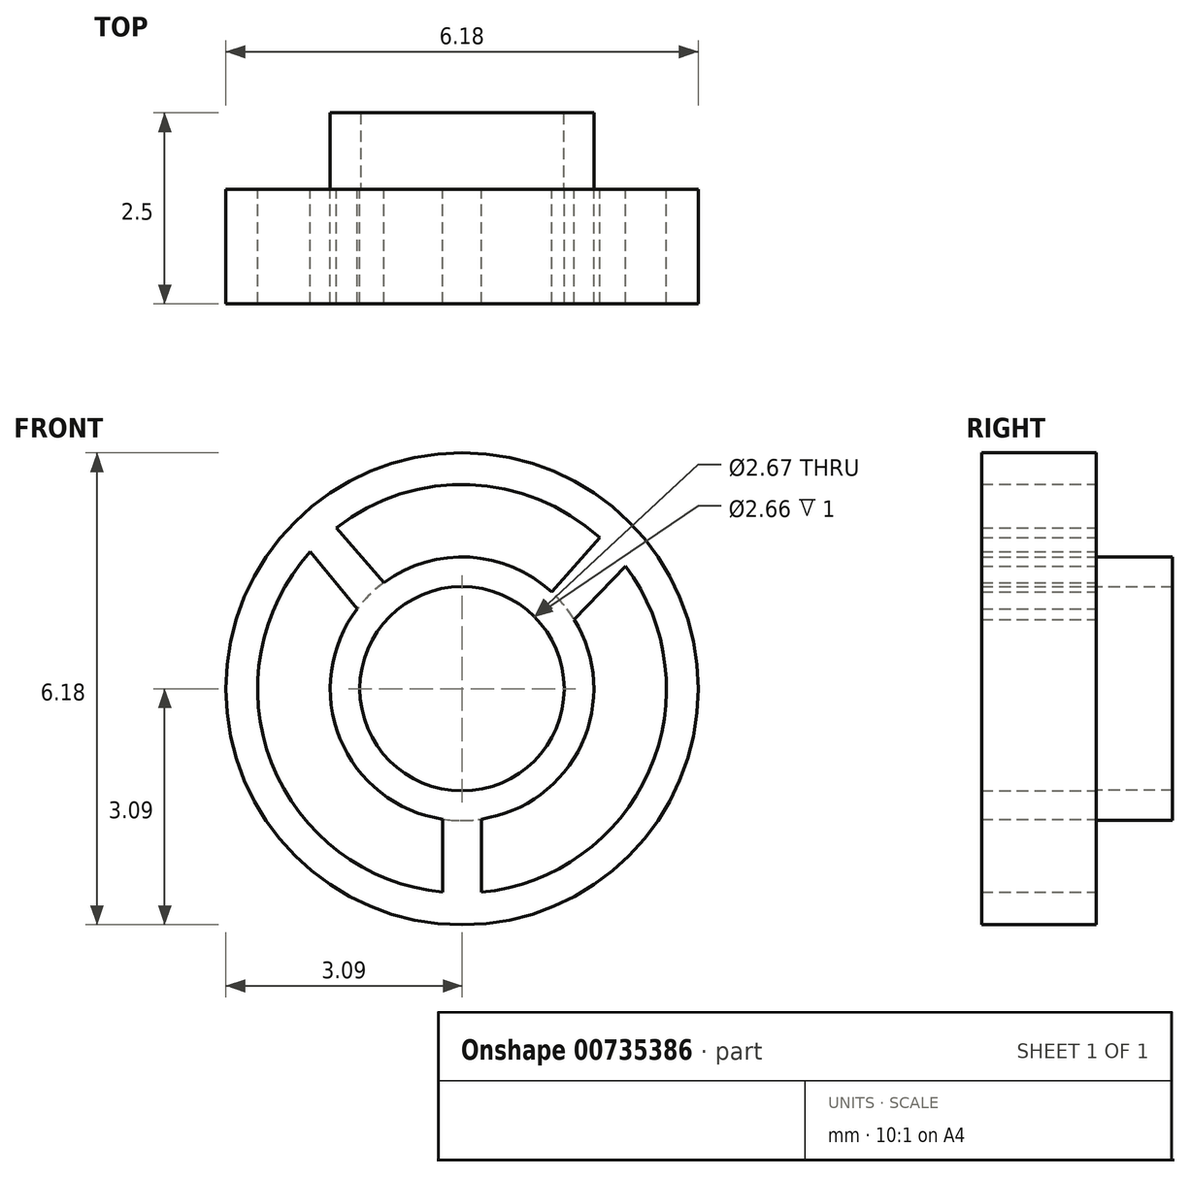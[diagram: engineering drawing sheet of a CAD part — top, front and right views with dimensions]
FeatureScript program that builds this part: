
annotation { "Feature Type Name" : "Feature", "Feature Type Description" : "" }
export const myFeature = defineFeature(function(context is Context, id is Id, definition is map)
    precondition{}
    {
        {
            var Q0;
            Q0=qCreatedBy(makeId("Front.planeOp"),FACE);
            var sketch = newSketch(context, id + "F0", { "sketchPlane" : qUnion([Q0])});
            skCircle(sketch, "E0", {"center": v(0, 0) * mm, "radius": 1.34 * mm});
            skCircle(sketch, "E1", {"center": v(0, 0) * mm, "radius": 1.73 * mm});
            skCircle(sketch, "E2", {"center": v(0, 0) * mm, "radius": 2.68 * mm});
            skCircle(sketch, "E3", {"center": v(0, 0) * mm, "radius": 3.1 * mm});
            skLineSegment(sketch, "E4", {"start": v(-1.02, 1.4) * mm, "end": v(-1.65, 2.1) * mm});
            skLineSegment(sketch, "E5", {"start": v(-1.37, 1.05) * mm, "end": v(-1.98, 1.8) * mm});
            skLineSegment(sketch, "E6", {"start": v(1.17, 1.27) * mm, "end": v(1.8, 1.98) * mm});
            skLineSegment(sketch, "E7", {"start": v(1.47, 0.9) * mm, "end": v(2.14, 1.6) * mm});
            skLineSegment(sketch, "E8", {"start": v(-0.25, -1.7) * mm, "end": v(-0.25, -2.66) * mm});
            skLineSegment(sketch, "E9", {"start": v(0.25, -1.7) * mm, "end": v(0.25, -2.66) * mm});
            skSolve(sketch);
        }
        {
            var Q0;
            Q0 = qSketchRegion(id + "F0", true);
            var Q1;
            {var subQ0=sQuery(id+"F0.wireOp",EDGE,"E4");Q1=makeQuery(id+"F0.imprint","IMPRINT",FACE,{"disambiguationData":[TD([[makeQuery(id+"F0.imprint","IMPRINT",EDGE,{"derivedFrom":subQ0}),1.0]])]});}
            var Q2;
            {var subQ0=sQuery(id+"F0.wireOp",EDGE,"E6");Q2=makeQuery(id+"F0.imprint","IMPRINT",FACE,{"disambiguationData":[TD([[makeQuery(id+"F0.imprint","IMPRINT",EDGE,{"derivedFrom":subQ0}),-1.0]])]});}
            var Q3;
            Q3=makeQuery(id+"F0.imprint","IMPRINT",FACE,{"disambiguationData":[TD([[makeQuery(id+"F0.imprint","IMPRINT",EDGE,{"derivedFrom":sQuery(id+"F0.wireOp",EDGE,"E0")}),-1.0]])]});
            var Q4;
            {var subQ0=sQuery(id+"F0.wireOp",EDGE,"E8");Q4=makeQuery(id+"F0.imprint","IMPRINT",FACE,{"disambiguationData":[TD([[makeQuery(id+"F0.imprint","IMPRINT",EDGE,{"derivedFrom":subQ0}),1.0]])]});}
            extrude(context, id + "F1", {"entities" : qUnion([Q0, Q1, Q2, Q3, Q4]), "depth" : 1.5 * mm, "offsetDistance" : 25 * mm});
        }
        {
            var Q0;
            Q0=makeQuery(id+"F1.opExtrude","CAP_FACE",FACE,{"disambiguationData":[OSD([sQuery(id+"F0.wireOp",EDGE,"E0"),sQuery(id+"F0.wireOp",EDGE,"E1"),sQuery(id+"F0.wireOp",EDGE,"E2"),sQuery(id+"F0.wireOp",EDGE,"E3"),sQuery(id+"F0.wireOp",EDGE,"E4"),sQuery(id+"F0.wireOp",EDGE,"E5"),sQuery(id+"F0.wireOp",EDGE,"E6"),sQuery(id+"F0.wireOp",EDGE,"E7"),sQuery(id+"F0.wireOp",EDGE,"E8"),sQuery(id+"F0.wireOp",EDGE,"E9")])],"isStart":true});
            var sketch = newSketch(context, id + "F2", { "sketchPlane" : qUnion([Q0])});
            skCircle(sketch, "E10", {"center": v(0, 0) * mm, "radius": 1.33 * mm});
            skCircle(sketch, "E11", {"center": v(0, 0) * mm, "radius": 1.73 * mm});
            skSolve(sketch);
        }
        {
            var Q0;
            Q0 = qSketchRegion(id + "F2", true);
            extrude(context, id + "F3", {"entities" : qUnion([Q0]), "operationType" : NewBodyOperationType.ADD, "depth" : 1 * mm, "offsetDistance" : 25 * mm});
        }
    });
